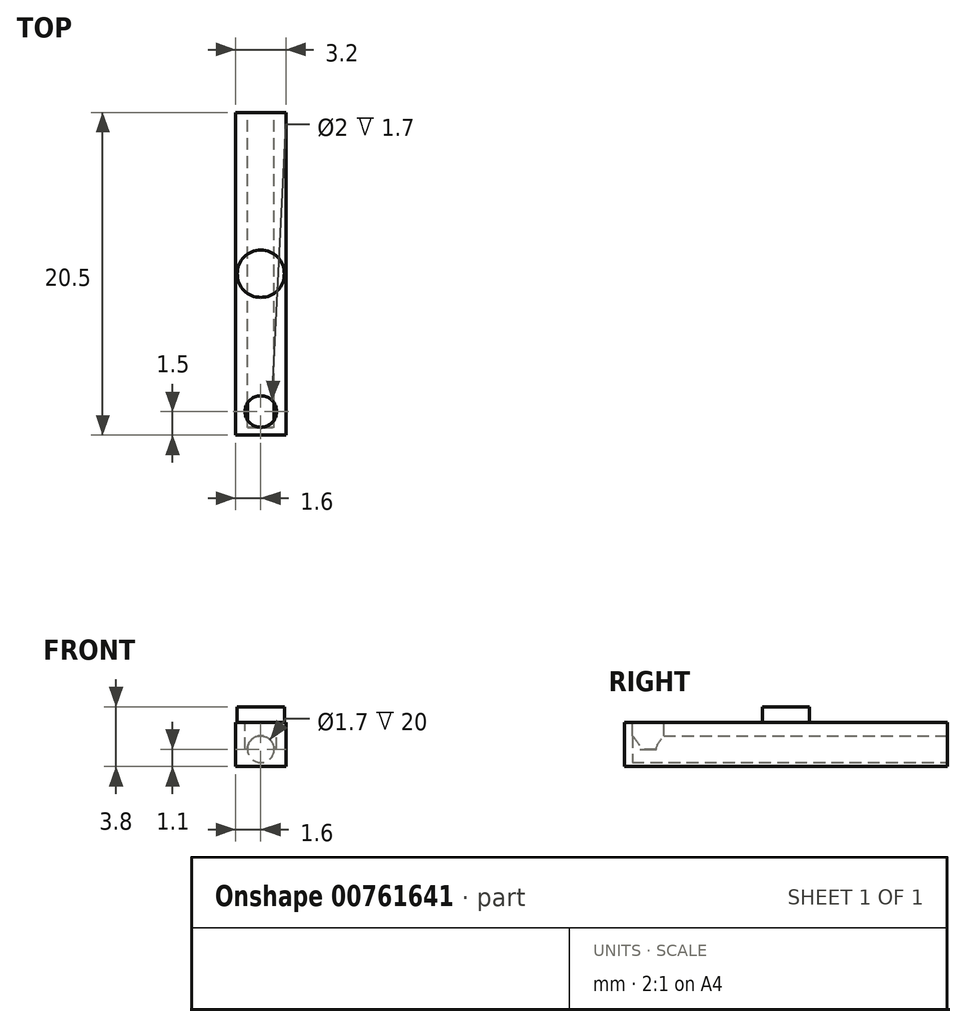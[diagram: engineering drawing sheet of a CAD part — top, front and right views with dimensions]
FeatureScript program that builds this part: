
annotation { "Feature Type Name" : "Feature", "Feature Type Description" : "" }
export const myFeature = defineFeature(function(context is Context, id is Id, definition is map)
    precondition{}
    {
        {
            var Q0;
            Q0=qCreatedBy(makeId("Top.planeOp"),FACE);
            var sketch = newSketch(context, id + "F0", { "sketchPlane" : qUnion([Q0])});
            skLineSegment(sketch, "E0.bottom", {"start": v(0, 0) * mm, "end": v(3.2, 0) * mm});
            skLineSegment(sketch, "E0.top", {"start": v(0, 20.5) * mm, "end": v(3.2, 20.5) * mm});
            skLineSegment(sketch, "E0.left", {"start": v(0, 0) * mm, "end": v(0, 20.5) * mm});
            skLineSegment(sketch, "E0.right", {"start": v(3.2, 0) * mm, "end": v(3.2, 20.5) * mm});
            skSolve(sketch);
        }
        {
            var Q0;
            Q0 = qSketchRegion(id + "F0", true);
            extrude(context, id + "F1", {"entities" : qUnion([Q0]), "depth" : 2.8 * mm, "offsetDistance" : 25 * mm});
        }
        {
            var Q0;
            Q0=makeQuery(id+"F1.opExtrude","SWEPT_FACE",FACE,{"disambiguationData":[OSD([sQuery(id+"F0.wireOp",EDGE,"E0.top")])]});
            var sketch = newSketch(context, id + "F2", { "sketchPlane" : qUnion([Q0])});
            skLineSegment(sketch, "E1.0", {"start": v(0, 0) * mm, "end": v(-3.2, 0) * mm, "construction": true});
            skLineSegment(sketch, "E2", {"start": v(-1.6, 0) * mm, "end": v(-1.6, 1.1) * mm, "construction": true});
            skCircle(sketch, "E3", {"center": v(-1.6, 1.1) * mm, "radius": 0.85 * mm});
            skSolve(sketch);
        }
        {
            var Q0;
            Q0 = qSketchRegion(id + "F2", true);
            extrude(context, id + "F3", {"entities" : qUnion([Q0]), "operationType" : NewBodyOperationType.REMOVE, "oppositeDirection" : true, "depth" : 20 * mm, "offsetDistance" : 25 * mm});
        }
        {
            var Q0;
            Q0=makeQuery(id+"F1.opExtrude","CAP_FACE",FACE,{"disambiguationData":[OSD([sQuery(id+"F0.wireOp",EDGE,"E0.bottom"),sQuery(id+"F0.wireOp",EDGE,"E0.top"),sQuery(id+"F0.wireOp",EDGE,"E0.left"),sQuery(id+"F0.wireOp",EDGE,"E0.right")])],"isStart":false});
            var sketch = newSketch(context, id + "F4", { "sketchPlane" : qUnion([Q0])});
            skLineSegment(sketch, "E4.0", {"start": v(0, 20.5) * mm, "end": v(3.2, 20.5) * mm, "construction": true});
            skLineSegment(sketch, "E5.0", {"start": v(0, 0) * mm, "end": v(3.2, 0) * mm, "construction": true});
            skLineSegment(sketch, "E6", {"start": v(1.6, 0) * mm, "end": v(1.6, 1.5) * mm, "construction": true});
            skCircle(sketch, "E7", {"center": v(1.6, 1.5) * mm, "radius": 1 * mm});
            skSolve(sketch);
        }
        {
            var Q0;
            Q0 = qSketchRegion(id + "F4", true);
            extrude(context, id + "F5", {"entities" : qUnion([Q0]), "operationType" : NewBodyOperationType.REMOVE, "oppositeDirection" : true, "depth" : 1.7 * mm, "offsetDistance" : 25 * mm});
        }
        {
            var Q0;
            Q0=makeQuery(id+"F1.opExtrude","CAP_FACE",FACE,{"disambiguationData":[OSD([sQuery(id+"F0.wireOp",EDGE,"E0.bottom"),sQuery(id+"F0.wireOp",EDGE,"E0.top"),sQuery(id+"F0.wireOp",EDGE,"E0.left"),sQuery(id+"F0.wireOp",EDGE,"E0.right")])],"isStart":false});
            var sketch = newSketch(context, id + "F6", { "sketchPlane" : qUnion([Q0])});
            skLineSegment(sketch, "E8.0", {"start": v(0, 20.5) * mm, "end": v(3.2, 20.5) * mm});
            skLineSegment(sketch, "E9.0", {"start": v(0, 0) * mm, "end": v(3.2, 0) * mm});
            skLineSegment(sketch, "E10", {"start": v(1.6, 0) * mm, "end": v(1.6, 10.25) * mm, "construction": true});
            skCircle(sketch, "E11", {"center": v(1.6, 10.25) * mm, "radius": 1.5 * mm});
            skSolve(sketch);
        }
        {
            var Q0;
            Q0 = qSketchRegion(id + "F6", true);
            extrude(context, id + "F7", {"entities" : qUnion([Q0]), "operationType" : NewBodyOperationType.ADD, "depth" : 1 * mm, "offsetDistance" : 25 * mm});
        }
    });
